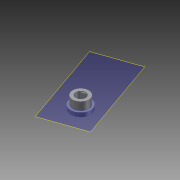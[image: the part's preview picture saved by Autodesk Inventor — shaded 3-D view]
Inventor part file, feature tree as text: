
AUTODESK INVENTOR PART (.ipt)
format: ipt  version: 2012 (Build 160160000, 160)  size: 713,728 bytes
history: native  units: mm
features: extrude x9, sketch x9, other x3, projected_geometry x3, plane x1, reference x1
ambient origin geometry x8: Origin, YZ Plane, XZ Plane, XY Plane, X Axis, Y Axis, Z Axis, Center Point
bodies: Solid1 (feature_tree)
feature tree (26):
  other  "Spur Gear2"
  extrude  "Extrusion1"  Depth=10.0mm TaperAngle=0.0deg
  extrude  "Extrusion2"  Depth=3.570646mm
  extrude  "Extrusion3"  Depth=0.3mm
  plane  "Work Plane1"
  extrude  "Extrusion4"  Depth=2.0mm
  extrude  "Extrusion5"  Depth=1.0mm
  extrude  "Extrusion6"  Depth=0.3mm TaperAngle=0.0deg
  extrude  "Extrusion7"  TaperAngle=0.0deg  [1 undecoded]
  sketch  "Sketch9"  dims[d22=4.0mm d23=0.0mm d24=4.0mm d25=0.0mm]
  extrude  "Extrusion8"  Depth=4.0mm TaperAngle=0.0deg
  extrude  "Extrusion9"  [1 undecoded]
  other  "Solid1::Spur Gear2"
  other  "TaggingFeature1"
  sketch  "Sketch2"  dims[d0=10.0mm d1=10.0mm d2=0.0mm]
  projected_geometry  "Projected Loop1"
  sketch  "Sketch3"  dims[d3=6.0mm d4=3.570646mm]
  sketch  "Sketch4"  dims[d6=0.3mm d7=0.3mm]
  sketch  "Sketch5"  dims[d8=10.0mm d9=0.0mm d10=2.0mm]
  reference  "Reference1"
  sketch  "Sketch6"  dims[d11=8.0mm d12=0.0mm d13=1.0mm]
  sketch  "Sketch7"  dims[d14=3.0mm d15=0.0mm d16=0.3mm d17=0.0mm]
  sketch  "Sketch8"  dims[d18=0.5mm d19=0.0mm d20=0.0mm d21=0.0mm]
  projected_geometry  "Projected Loop2"
  sketch  "Sketch10"
  projected_geometry  "Projected Loop3"
note: 2 required parameter values undecoded (feature->parameter linkage not recoverable at this tier; creation-order binding heuristic only, values carry confidence <= 0.55)
